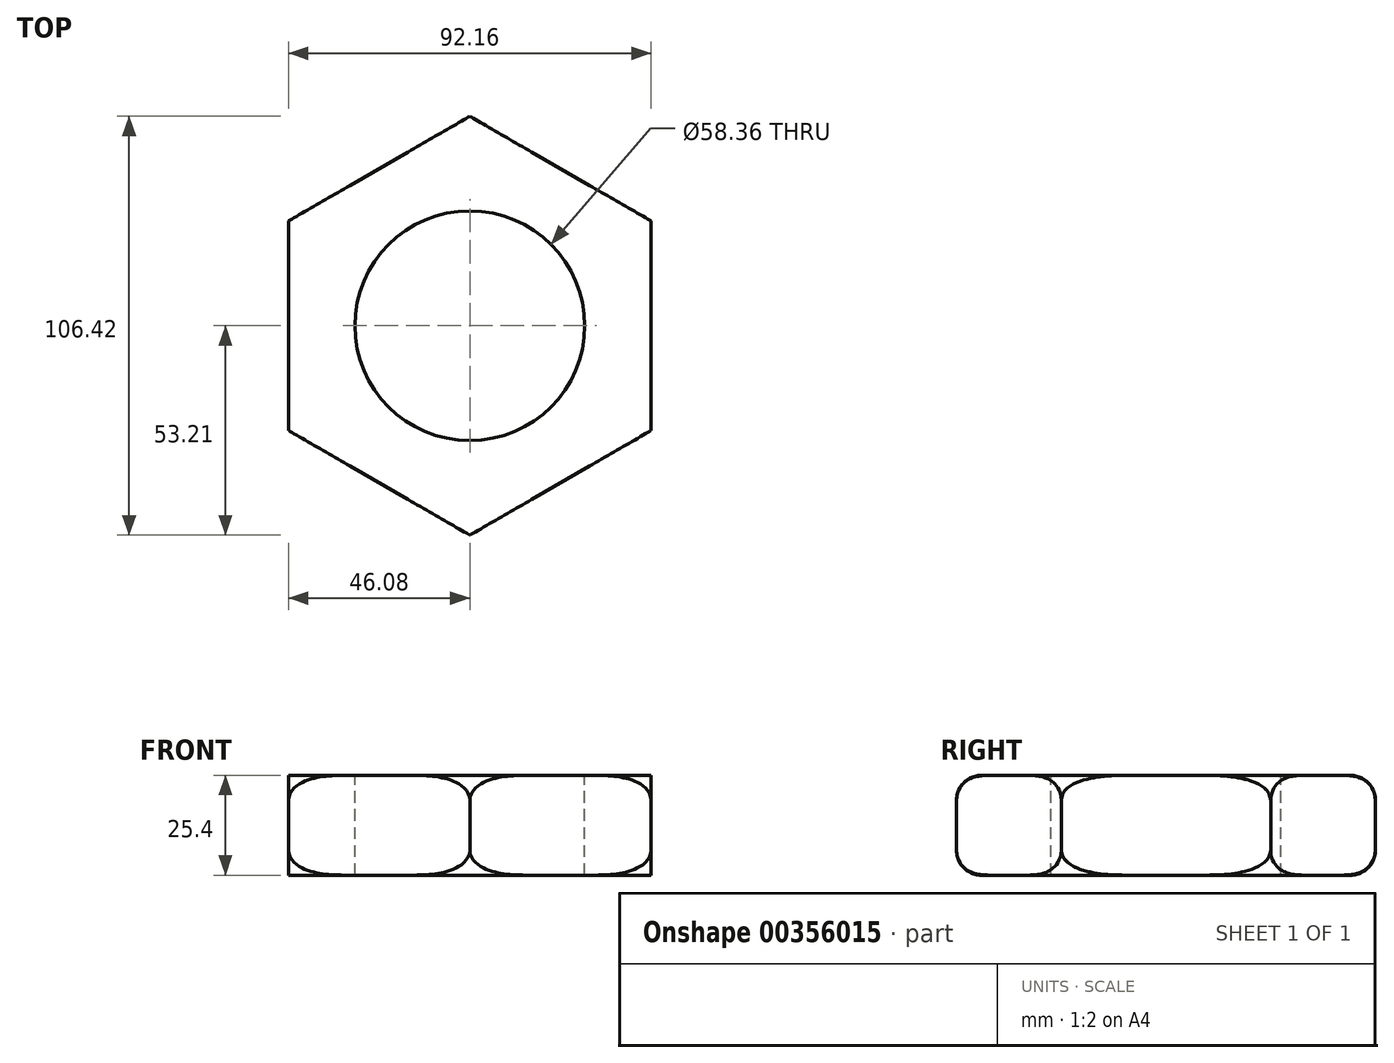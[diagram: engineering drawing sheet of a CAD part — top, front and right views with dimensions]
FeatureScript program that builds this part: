
annotation { "Feature Type Name" : "Feature", "Feature Type Description" : "" }
export const myFeature = defineFeature(function(context is Context, id is Id, definition is map)
    precondition{}
    {
        {
            var Q0;
            Q0=qCreatedBy(makeId("Top.planeOp"),FACE);
            var sketch = newSketch(context, id + "F0", { "sketchPlane" : qUnion([Q0])});
            skCircle(sketch, "E0.cCircle", {"center": v(0, 0) * mm, "radius": 46.08 * mm, "construction": true});
            skLineSegment(sketch, "E0.0", {"start": v(46.08, 26.6) * mm, "end": v(46.08, -26.6) * mm});
            skLineSegment(sketch, "E0.1", {"start": v(46.08, -26.6) * mm, "end": v(0, -53.2) * mm});
            skLineSegment(sketch, "E0.2", {"start": v(0, -53.2) * mm, "end": v(-46.08, -26.6) * mm});
            skLineSegment(sketch, "E0.3", {"start": v(-46.08, -26.6) * mm, "end": v(-46.08, 26.6) * mm});
            skLineSegment(sketch, "E0.4", {"start": v(-46.08, 26.6) * mm, "end": v(0, 53.2) * mm});
            skLineSegment(sketch, "E0.5", {"start": v(0, 53.2) * mm, "end": v(46.08, 26.6) * mm});
            skPoint(sketch, "E0.0.midPoint", {"position": v(46.08, 0) * mm});
            skSolve(sketch);
        }
        {
            var Q0;
            Q0=makeQuery(id+"F0.imprint","IMPRINT",FACE,{"disambiguationData":[TD([[makeQuery(id+"F0.imprint","IMPRINT",EDGE,{"derivedFrom":sQuery(id+"F0.wireOp",EDGE,"E0.0")}),-1.0]])]});
            extrude(context, id + "F1", {"entities" : qUnion([Q0]), "depth" : 25.4 * mm});
        }
        {
            var Q0;
            Q0=makeQuery(id+"F1.opExtrude","CAP_FACE",FACE,{"disambiguationData":[OSD([sQuery(id+"F0.wireOp",EDGE,"E0.0"),sQuery(id+"F0.wireOp",EDGE,"E0.1"),sQuery(id+"F0.wireOp",EDGE,"E0.2"),sQuery(id+"F0.wireOp",EDGE,"E0.3"),sQuery(id+"F0.wireOp",EDGE,"E0.4"),sQuery(id+"F0.wireOp",EDGE,"E0.5")])],"isStart":false});
            var sketch = newSketch(context, id + "F2", { "sketchPlane" : qUnion([Q0])});
            skCircle(sketch, "E1", {"center": v(0, 0) * mm, "radius": 29.18 * mm});
            skSolve(sketch);
        }
        {
            var Q0;
            Q0=makeQuery(id+"F2.imprint","IMPRINT",FACE,{"disambiguationData":[TD([[makeQuery(id+"F2.imprint","IMPRINT",EDGE,{"derivedFrom":sQuery(id+"F2.wireOp",EDGE,"E1")}),1.0]])]});
            var Q1;
            Q1=sQuery(id+"F2.wireOp",EDGE,"E1");
            extrude(context, id + "F3", {"entities" : qUnion([Q0]), "operationType" : NewBodyOperationType.REMOVE, "surfaceEntities" : qUnion([Q1]), "oppositeDirection" : true, "depth" : 25.4 * mm});
        }
        {
            var Q0;
            Q0=qCreatedBy(makeId("Right.planeOp"),FACE);
            var sketch = newSketch(context, id + "F4", { "sketchPlane" : qUnion([Q0])});
            skLineSegment(sketch, "E2", {"start": v(46.86, 25.4) * mm, "end": v(53.2, 25.4) * mm});
            skLineSegment(sketch, "E3", {"start": v(53.2, 25.4) * mm, "end": v(53.2, 19.05) * mm});
            skArc(sketch, "E4", {"start": v(53.2, 19.05) * mm, "mid": v(51.35, 23.54) * mm, "end": v(46.86, 25.4) * mm});
            skLineSegment(sketch, "E5", {"start": v(53.2, 6.35) * mm, "end": v(53.2, 0) * mm});
            skLineSegment(sketch, "E6", {"start": v(46.86, 0) * mm, "end": v(53.2, 0) * mm});
            skArc(sketch, "E7", {"start": v(46.86, 0) * mm, "mid": v(51.35, 1.86) * mm, "end": v(53.2, 6.35) * mm});
            skSolve(sketch);
        }
        {
            var Q0;
            Q0=makeQuery(id+"F4.imprint","IMPRINT",FACE,{"disambiguationData":[TD([[makeQuery(id+"F4.imprint","IMPRINT",EDGE,{"derivedFrom":sQuery(id+"F4.wireOp",EDGE,"E2")}),-1.0]])]});
            var Q1;
            Q1=makeQuery(id+"F3.boolean.opBoolean","COPY",FACE,{"derivedFrom":makeQuery(id+"F3.opExtrude","SWEPT_FACE",FACE,{"disambiguationData":[OSD([sQuery(id+"F2.wireOp",EDGE,"E1")])]})});
            revolve(context, id + "F5", {"operationType" : NewBodyOperationType.REMOVE, "entities" : qUnion([Q0]), "axis" : qUnion([Q1]), "revolveType" : RevolveType.FULL, "oppositeDirection" : true});
        }
        {
            var Q0;
            Q0=qCreatedBy(makeId("Right.planeOp"),FACE);
            var sketch = newSketch(context, id + "F6", { "sketchPlane" : qUnion([Q0])});
            skLineSegment(sketch, "E8", {"start": v(53.2, 6.35) * mm, "end": v(53.2, 0) * mm});
            skLineSegment(sketch, "E9", {"start": v(46.86, 0) * mm, "end": v(53.2, 0) * mm});
            skArc(sketch, "E10", {"start": v(46.86, 0) * mm, "mid": v(51.35, 1.86) * mm, "end": v(53.2, 6.35) * mm});
            skSolve(sketch);
        }
        {
            var Q0;
            Q0=makeQuery(id+"F6.imprint","IMPRINT",FACE,{"disambiguationData":[TD([[makeQuery(id+"F6.imprint","IMPRINT",EDGE,{"derivedFrom":sQuery(id+"F6.wireOp",EDGE,"E8")}),-1.0]])]});
            var Q1;
            Q1=makeQuery(id+"F3.boolean.opBoolean","COPY",FACE,{"derivedFrom":makeQuery(id+"F3.opExtrude","SWEPT_FACE",FACE,{"disambiguationData":[OSD([sQuery(id+"F2.wireOp",EDGE,"E1")])]})});
            revolve(context, id + "F7", {"operationType" : NewBodyOperationType.REMOVE, "entities" : qUnion([Q0]), "axis" : qUnion([Q1]), "revolveType" : RevolveType.FULL, "oppositeDirection" : true});
        }
    });
